AUTODESK INVENTOR PART (.ipt)
format: ipt  version: 2018 (Build 220112000, 112)  size: 118,272 bytes
history: native  units: in
note: dims shown in document units (in); Inventor stores cm internally (conversion verified against a paired STEP export)
features: sketch x1
ambient origin geometry x8: Origin, YZ Plane, XZ Plane, XY Plane, X Axis, Y Axis, Z Axis, Center Point
feature tree (1):
  sketch  "Sketch1"  dims[d1=10.5in d2=5.0in d4=45.0deg d6=0.0327in d7=1.2041in d9=0.0327in d10=2.5in d11=5.25in d12=0.125in d13=135.0deg d14=0.125in d16=135.0deg d17=0.125in d18=2.5in d19=1.2041in d20=45.0deg d21=45.0deg d22=1.25in d23=1.25in d24=2.375in d25=5.25in d26=0.125in d27=0.9045in d29=1.2012in d30=2.625in d31=1.875in d32=0.5in]
